# Revit family: Power-ModularDevices-GEWISS-90AM-CONTACTORS_MANUAL_COMMAND_25A
name_source: partatom
category: Apparecchi elettrici
revit_build: Autodesk Revit 2016 (Build: 20161004_0715(x64)
units: mm (PartAtom-declared; Revit-internal decimal feet)

## family parameters
Condiviso = No
Host = Superficie
Mantenere orientamento annotazione = Sì
Numero OmniClass = 23.80.30.00
Punto di calcolo locali = Sì
Quota connettore circolare = Usa diametro
Taglio con vuoti quando caricato = No
Tipo di parte = Normale
Titolo OmniClass = Distribution Devices

## types (4) — shared parameters
A = 36 mm  [stored 0.11811 ft]
B = 85 mm  [stored 0.278871 ft]
C = 65 mm  [stored 0.213255 ft]
Catalogue = POWER
Catalogue Range = 90 AM
Control = Manual
D = 45 mm  [stored 0.147638 ft]
Electrocod = 1712
Fin_contatore = <Per categoria>
IDF = a233116f-77d4-4d3b-91b6-67c450f5d48b
IDT = ba8551de-7667-4587-b6d7-311e7f73038c
Immagine tipo = GWD6754.jpg
No. Chorus modules = 2
Numero poli = 1
Potenza in Watt = 0 V
Produttore = GEWISS S.p.A.
Prospetto di default = 1219 mm
Rated current (AC-1/AC-7a) = 25 A - CTRM25
TEXT LABEL = A
Technical sheet = https://www.gewiss.com
URL = https://www.gewiss.com
Version file RFA = 18.0

## per-type parameters (varying)
| type | Control coil voltage (V) | Descrizione | EAN code | Modello |
| GWD6752 - CONTACTOR D/N 25A 3NO 230V 2M | 230Vac - 220Vdc | CONTACTOR D/N 25A 3NO 230V 2M | 8011564809543 | GWD6752 |
| GWD6753 - CONTACTOR D/N 25A 4NO 24V 2M | 24Vac/dc | CONTACTOR D/N 25A 4NO 24V 2M | 8011564809550 | GWD6753 |
| GWD6754 - CONTACTOR D/N 25A 4NO 230V 2M | 230Vac - 220Vdc | CONTACTOR D/N 25A 4NO 230V 2M | 8011564809567 | GWD6754 |
| GWD6751 - CONTACTOR D/N 25A 2NO 230V 2M | 230Vac - 220Vdc | CONTACTOR D/N 25A 2NO 230V 2M | 8011564809536 | GWD6751 |

note: [stored X ft] marks values corroborated as IEEE doubles in the binary element streams (Revit-internal decimal feet)
